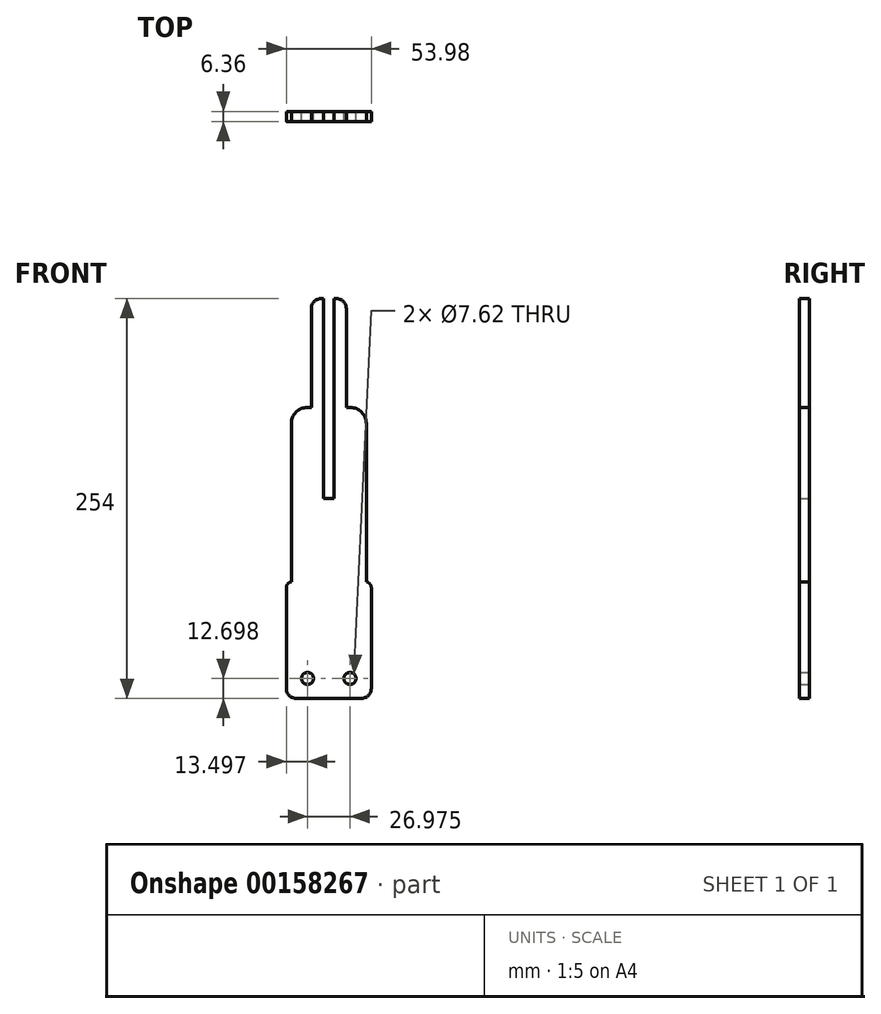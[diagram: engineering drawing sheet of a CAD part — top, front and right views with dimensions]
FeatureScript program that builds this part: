
annotation { "Feature Type Name" : "Feature", "Feature Type Description" : "" }
export const myFeature = defineFeature(function(context is Context, id is Id, definition is map)
    precondition{}
    {
        {
            var Q0;
            Q0=qCreatedBy(makeId("Front.planeOp"),FACE);
            var sketch = newSketch(context, id + "F0", { "sketchPlane" : qUnion([Q0])});
            skLineSegment(sketch, "E0.bottom", {"start": v(-52.29, -23.33) * mm, "end": v(-49.11, -23.33) * mm});
            skLineSegment(sketch, "E0.top", {"start": v(-52.29, -97.44) * mm, "end": v(1.69, -97.44) * mm});
            skLineSegment(sketch, "E0.left", {"start": v(-52.29, -23.33) * mm, "end": v(-52.29, -97.44) * mm});
            skLineSegment(sketch, "E0.right", {"start": v(1.69, -23.33) * mm, "end": v(1.69, -97.44) * mm});
            skLineSegment(sketch, "E1.bottom", {"start": v(-49.11, 87.37) * mm, "end": v(-36.41, 87.37) * mm});
            skLineSegment(sketch, "E1.left", {"start": v(-49.11, 87.37) * mm, "end": v(-49.11, -23.33) * mm});
            skLineSegment(sketch, "E1.right", {"start": v(-1.49, 87.37) * mm, "end": v(-1.49, -23.33) * mm});
            skLineSegment(sketch, "E2.bottom", {"start": v(-36.41, 156.56) * mm, "end": v(-28.47, 156.56) * mm});
            skLineSegment(sketch, "E2.left", {"start": v(-36.41, 156.56) * mm, "end": v(-36.41, 87.37) * mm});
            skLineSegment(sketch, "E2.right", {"start": v(-14.19, 156.56) * mm, "end": v(-14.19, 87.37) * mm});
            skLineSegment(sketch, "E3.trimOffspring", {"start": v(-1.49, -23.33) * mm, "end": v(1.69, -23.33) * mm});
            skLineSegment(sketch, "E4.trimOffspring", {"start": v(-14.19, 87.37) * mm, "end": v(-1.49, 87.37) * mm});
            skCircle(sketch, "E5", {"center": v(-38.8, -84.74) * mm, "radius": 3.81 * mm});
            skCircle(sketch, "E6", {"center": v(-11.82, -84.74) * mm, "radius": 3.81 * mm});
            skLineSegment(sketch, "E7.top", {"start": v(-28.47, 29.56) * mm, "end": v(-22.12, 29.56) * mm});
            skLineSegment(sketch, "E7.left", {"start": v(-28.47, 156.56) * mm, "end": v(-28.47, 29.56) * mm});
            skLineSegment(sketch, "E7.right", {"start": v(-22.12, 156.56) * mm, "end": v(-22.12, 29.56) * mm});
            skLineSegment(sketch, "E8.trimOffspring", {"start": v(-22.12, 156.56) * mm, "end": v(-14.19, 156.56) * mm});
            skSolve(sketch);
        }
        {
            var Q0;
            Q0=makeQuery(id+"F0.imprint","IMPRINT",FACE,{"disambiguationData":[TD([[makeQuery(id+"F0.imprint","IMPRINT",EDGE,{"derivedFrom":sQuery(id+"F0.wireOp",EDGE,"E0.bottom")}),-1.0]])]});
            extrude(context, id + "F1", {"entities" : qUnion([Q0]), "endBound" : BoundingType.SYMMETRIC, "depth" : 6.35 * mm});
        }
        {
            var Q0;
            Q0=makeQuery(id+"F1.opExtrude","SWEPT_EDGE",EDGE,{"disambiguationData":[OSD([sQuery(id+"F0.wireOp",EDGE,"E1.right"),sQuery(id+"F0.wireOp",EDGE,"E4.trimOffspring")])]});
            var Q1;
            Q1=makeQuery(id+"F1.opExtrude","SWEPT_EDGE",EDGE,{"disambiguationData":[OSD([sQuery(id+"F0.wireOp",EDGE,"E1.bottom"),sQuery(id+"F0.wireOp",EDGE,"E1.left")])]});
            fillet(context, id + "F2", {"entities" : qUnion([Q0, Q1]), "radius" : 10.16 * mm, "tangentPropagation" : true, "allowEdgeOverflow" : false});
        }
        {
            var Q0;
            Q0=makeQuery(id+"F1.opExtrude","SWEPT_EDGE",EDGE,{"disambiguationData":[OSD([sQuery(id+"F0.wireOp",EDGE,"E2.right"),sQuery(id+"F0.wireOp",EDGE,"E8.trimOffspring")])]});
            var Q1;
            Q1=makeQuery(id+"F1.opExtrude","SWEPT_EDGE",EDGE,{"disambiguationData":[OSD([sQuery(id+"F0.wireOp",EDGE,"E2.bottom"),sQuery(id+"F0.wireOp",EDGE,"E2.left")])]});
            fillet(context, id + "F3", {"entities" : qUnion([Q0, Q1]), "radius" : 6.35 * mm, "tangentPropagation" : true, "allowEdgeOverflow" : false});
        }
        {
            var Q0;
            Q0=makeQuery(id+"F1.opExtrude","SWEPT_EDGE",EDGE,{"disambiguationData":[OSD([sQuery(id+"F0.wireOp",EDGE,"E0.bottom"),sQuery(id+"F0.wireOp",EDGE,"E0.left")])]});
            var Q1;
            Q1=makeQuery(id+"F1.opExtrude","SWEPT_EDGE",EDGE,{"disambiguationData":[OSD([sQuery(id+"F0.wireOp",EDGE,"E0.right"),sQuery(id+"F0.wireOp",EDGE,"E3.trimOffspring")])]});
            fillet(context, id + "F4", {"entities" : qUnion([Q0, Q1]), "radius" : 3.8 * mm, "tangentPropagation" : true, "allowEdgeOverflow" : false});
        }
        {
            var Q0;
            Q0=makeQuery(id+"F1.opExtrude","SWEPT_EDGE",EDGE,{"disambiguationData":[OSD([sQuery(id+"F0.wireOp",EDGE,"E0.top"),sQuery(id+"F0.wireOp",EDGE,"E0.left")])]});
            var Q1;
            Q1=makeQuery(id+"F1.opExtrude","SWEPT_EDGE",EDGE,{"disambiguationData":[OSD([sQuery(id+"F0.wireOp",EDGE,"E0.top"),sQuery(id+"F0.wireOp",EDGE,"E0.right")])]});
            fillet(context, id + "F5", {"entities" : qUnion([Q0, Q1]), "radius" : 6.35 * mm, "tangentPropagation" : true, "allowEdgeOverflow" : false});
        }
    });
